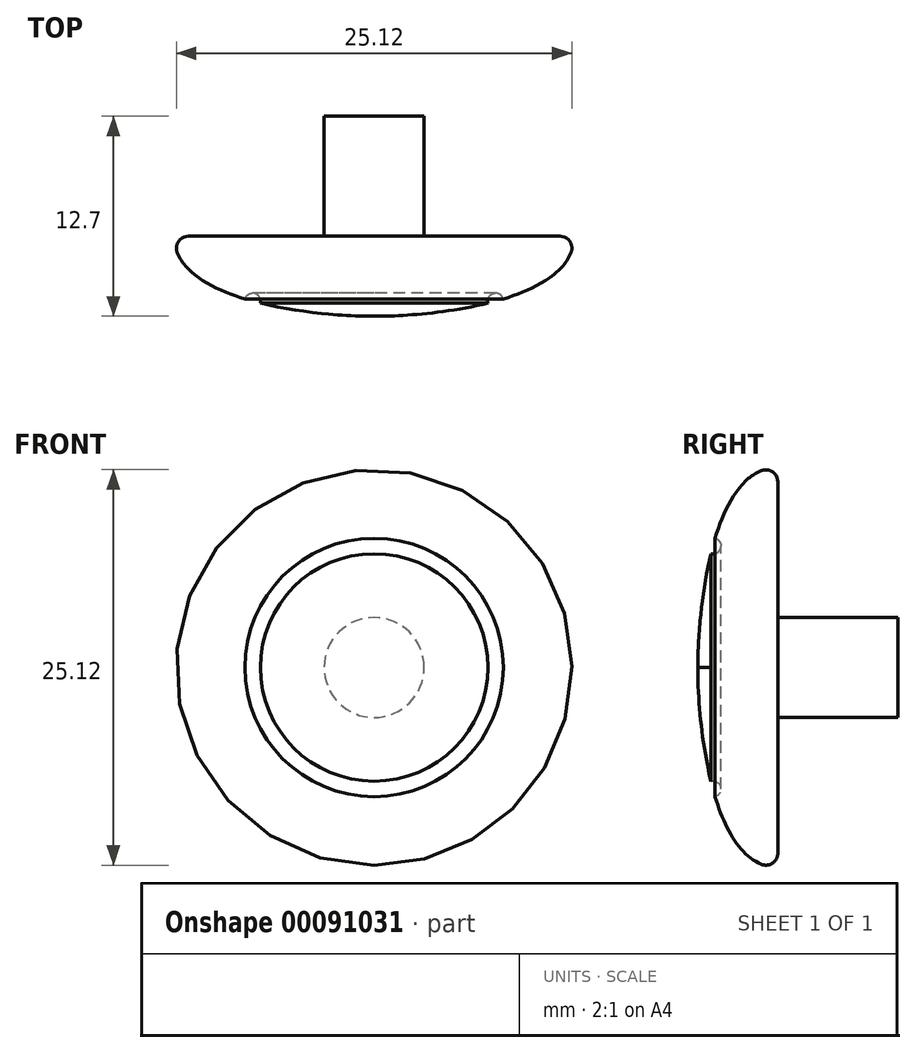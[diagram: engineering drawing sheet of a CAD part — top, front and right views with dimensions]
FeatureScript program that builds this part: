
annotation { "Feature Type Name" : "Feature", "Feature Type Description" : "" }
export const myFeature = defineFeature(function(context is Context, id is Id, definition is map)
    precondition{}
    {
        {
            var Q0;
            Q0=qCreatedBy(makeId("Top.planeOp"),FACE);
            var sketch = newSketch(context, id + "F0", { "sketchPlane" : qUnion([Q0])});
            skLineSegment(sketch, "E0", {"start": v(0, 0) * mm, "end": v(3.18, 0) * mm});
            skLineSegment(sketch, "E1", {"start": v(3.18, 0) * mm, "end": v(3.18, -7.62) * mm});
            skLineSegment(sketch, "E2", {"start": v(3.18, -7.62) * mm, "end": v(12.7, -7.62) * mm});
            skLineSegment(sketch, "E3", {"start": v(0, -12.7) * mm, "end": v(0, 0) * mm});
            skFitSpline(sketch, "E4", {"points": [v(0, -12.7) * mm, v(12.7, -7.62) * mm], "startDerivative": vector(7.34, -0.1) * mm, "endDerivative": vector(-0.12, 13.46) * mm});
            skArc(sketch, "E5", {"start": v(8.2, -11.6) * mm, "mid": v(7.58, -11.25) * mm, "end": v(7.23, -11.87) * mm});
            skSolve(sketch);
        }
        {
            var Q0;
            Q0=makeQuery(id+"F0.imprint","IMPRINT",FACE,{"disambiguationData":[TD([[makeQuery(id+"F0.imprint","IMPRINT",EDGE,{"derivedFrom":sQuery(id+"F0.wireOp",EDGE,"E0")}),-1.0]])]});
            var Q1;
            Q1=sQuery(id+"F0.wireOp",EDGE,"E3");
            revolve(context, id + "F1", {"entities" : qUnion([Q0]), "axis" : qUnion([Q1]), "revolveType" : RevolveType.FULL});
        }
        {
            var Q0;
            Q0=makeQuery(id+"F1.opRevolve","SWEPT_EDGE",EDGE,{"disambiguationData":[OSD([sQuery(id+"F0.wireOp",EDGE,"E2"),sQuery(id+"F0.wireOp",EDGE,"E4")])]});
            fillet(context, id + "F2", {"entities" : qUnion([Q0]), "radius" : 0.76 * mm, "tangentPropagation" : true, "allowEdgeOverflow" : false});
        }
    });
